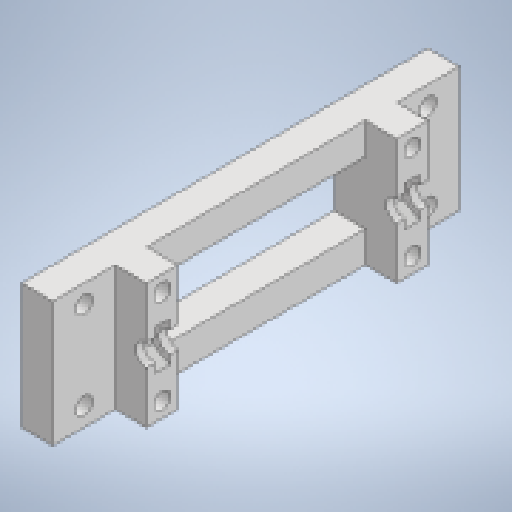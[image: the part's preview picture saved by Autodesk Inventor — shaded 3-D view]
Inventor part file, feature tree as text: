
AUTODESK INVENTOR PART (.ipt)
format: ipt  version: 2023 (Build 270158000, 158)  size: 273,920 bytes
history: native  units: mm
features: extrude x7, sketch x7, plane x2, mirror x1
ambient origin geometry x8: Origin, YZ Plane, XZ Plane, XY Plane, X Axis, Y Axis, Z Axis, Center Point
bodies: Solid1 (feature_tree)
feature tree (17):
  extrude  "Extrusion1"  Depth=5.0mm
  extrude  "Extrusion2"  Depth=15.0mm
  extrude  "Extrusion3"  Depth=35.0mm
  extrude  "Extrusion4"  Depth=10.0mm
  extrude  "Extrusion5"  Depth=10.0mm
  extrude  "Extrusion6"  Depth=200.0mm TaperAngle=0.0deg
  plane  "Work Plane1"
  extrude  "Extrusion7"  Depth=5.0mm
  plane  "Work Plane2"
  mirror  "Mirror1"
  sketch  "Sketch1"  dims[d0=5.0mm d1=5.0mm]
  sketch  "Sketch2"  dims[d2=5.0mm d3=15.0mm]
  sketch  "Sketch3"  dims[d4=15.0mm d5=35.0mm]
  sketch  "Sketch4"  dims[d6=20.0mm d7=0.0mm d8=10.0mm]
  sketch  "Sketch5"  dims[d9=10.0mm d10=10.0mm]
  sketch  "Sketch6"  dims[d11=3.5mm d12=200.0mm d13=0.0mm]
  sketch  "Sketch7"  dims[d14=5.0mm d15=5.0mm d16=20.0mm d17=0.0mm d18=10.0mm d19=10.0mm d20=3.0mm d21=3.0mm d22=5.0mm d23=5.0mm d24=5.0mm d25=5.0mm d26=3.0mm d27=3.0mm d28=2.75mm d29=2.75mm d30=2.75mm d31=2.75mm d32=5.0mm d33=0.0mm d34=2.5mm d35=2.5mm d36=2.5mm d37=2.5mm d38=2.5mm d39=2.5mm d40=2.5mm d41=2.5mm d42=2.7mm d43=2.7mm d44=2.7mm d45=2.7mm d46=15.0mm d47=0.0mm d48=4.7mm d49=4.7mm d50=4.7mm d51=4.7mm d52=7.5mm d53=0.0mm d57=20.0mm d58=2.4mm d59=0.0mm d60=2.75mm]
